# Revit family: TD92_BER711_MAR030_RVT20_R00
name_source: partatom
category: Mobiliário
units: mm (PartAtom-declared; Revit-internal decimal feet)

## family parameters
Com base no plano de trabalho = Não
Compartilhado = Não
Corte com vazios quando carregada = Não
Número OmniClass = 23.40.20.00
Ponto de cálculo do ambiente = Não
Sempre na vertical = Sim
Título OmniClass = General Furniture and Specialties

## types (1)
- TD92_BER711_MAR030_RVT20_R00
    Descrição = Perfeita para se adaptar a qualquer ambiente, seja escritório ou casa, a Poltrona Tramontina Berta em Polietileno pode suportar uma carga estática de 160 kg. Bela, confortável e resistente, ela certamente irá embelezar o seu ambiente.
    Elevação padrão = 0  [stored 0 ft]
    Fabricante = Tramontina Delta S.A
    Modelo = Poltrona Tramontina Berta em Polietileno Mariner
    Nota-chave = 92711030
    URL = https://www.tramontinastore.com

note: [stored X ft] marks values corroborated as IEEE doubles in the binary element streams (Revit-internal decimal feet)
